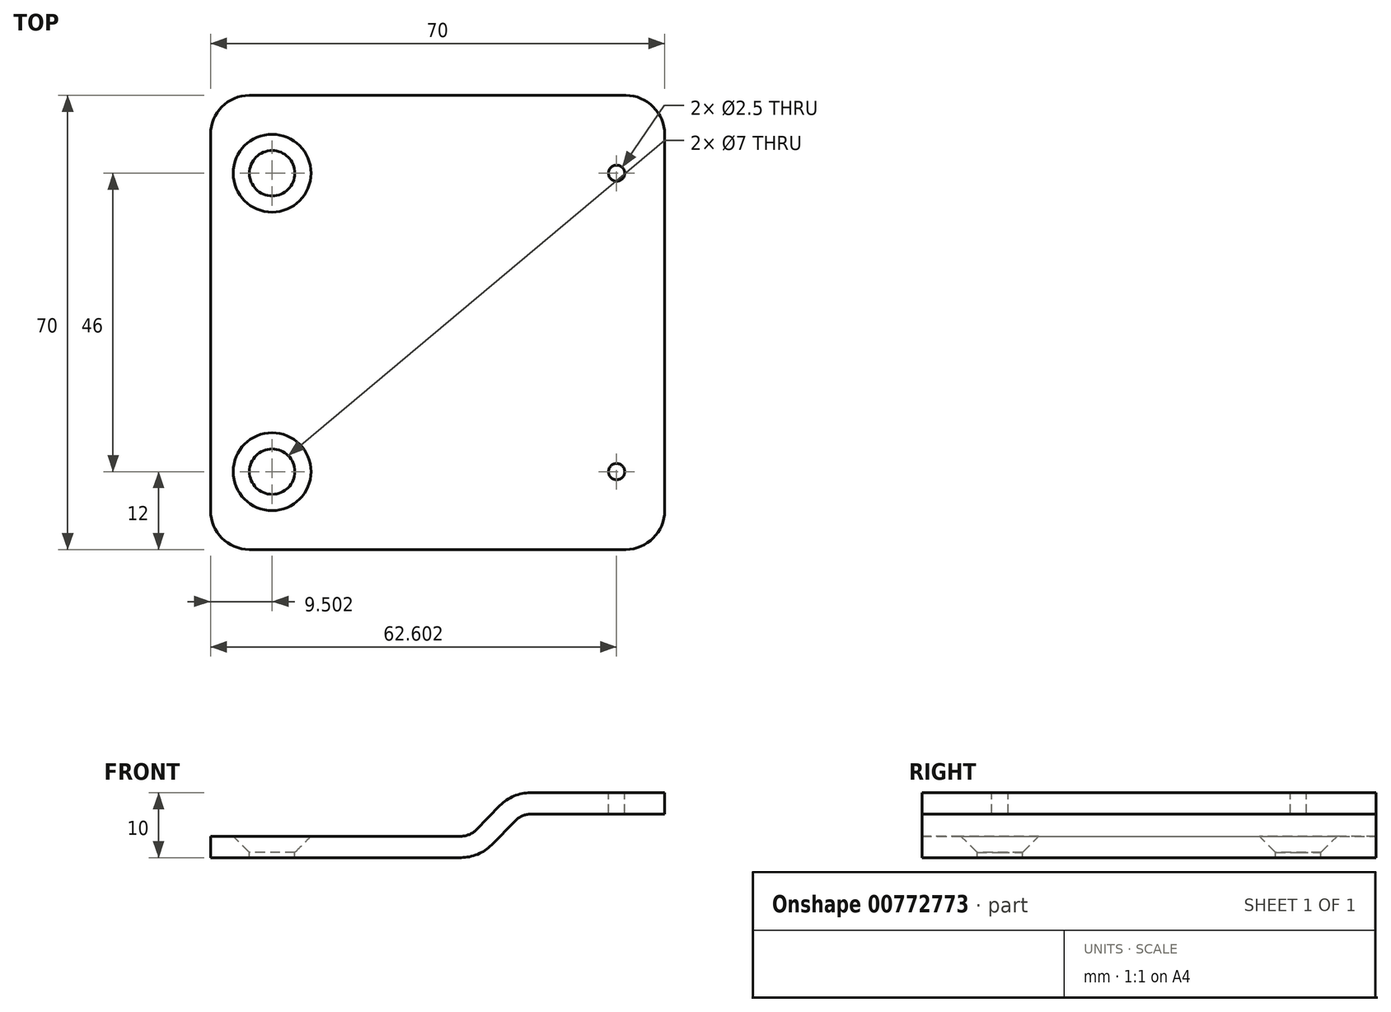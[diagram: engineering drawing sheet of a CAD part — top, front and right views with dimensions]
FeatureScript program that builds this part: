
annotation { "Feature Type Name" : "Feature", "Feature Type Description" : "" }
export const myFeature = defineFeature(function(context is Context, id is Id, definition is map)
    precondition{}
    {
        {
            var Q0;
            Q0=qCreatedBy(makeId("Front.planeOp"),FACE);
            var sketch = newSketch(context, id + "F0", { "sketchPlane" : qUnion([Q0])});
            skLineSegment(sketch, "E0", {"start": v(-30.2, 0) * mm, "end": v(-30.2, 3.3) * mm});
            skLineSegment(sketch, "E1", {"start": v(-30.2, 3.3) * mm, "end": v(8.41, 3.3) * mm});
            skLineSegment(sketch, "E2", {"start": v(10.77, 4.3) * mm, "end": v(14.42, 8.02) * mm});
            skLineSegment(sketch, "E3", {"start": v(19.14, 10) * mm, "end": v(39.8, 10) * mm});
            skLineSegment(sketch, "E4", {"start": v(39.8, 10) * mm, "end": v(39.8, 6.7) * mm});
            skLineSegment(sketch, "E5", {"start": v(-30.2, 0) * mm, "end": v(8.42, 0) * mm});
            skLineSegment(sketch, "E6", {"start": v(13.12, 1.96) * mm, "end": v(16.83, 5.72) * mm});
            skLineSegment(sketch, "E7", {"start": v(39.8, 6.7) * mm, "end": v(19.18, 6.7) * mm});
            skPoint(sketch, "E8.visualSharp", {"position": v(17.8, 6.7) * mm});
            skArc(sketch, "E8.filletArc", {"start": v(19.18, 6.7) * mm, "mid": v(17.9, 6.45) * mm, "end": v(16.83, 5.72) * mm});
            skPoint(sketch, "E9.visualSharp", {"position": v(9.8, 3.3) * mm});
            skArc(sketch, "E9.filletArc", {"start": v(8.41, 3.3) * mm, "mid": v(9.7, 3.56) * mm, "end": v(10.77, 4.3) * mm});
            skPoint(sketch, "E10.visualSharp", {"position": v(16.36, 10) * mm});
            skArc(sketch, "E10.filletArc", {"start": v(19.14, 10) * mm, "mid": v(16.58, 9.48) * mm, "end": v(14.42, 8.02) * mm});
            skPoint(sketch, "E11.visualSharp", {"position": v(11.18, 0) * mm});
            skArc(sketch, "E11.filletArc", {"start": v(8.42, 0) * mm, "mid": v(10.97, 0.5) * mm, "end": v(13.12, 1.96) * mm});
            skSolve(sketch);
        }
        {
            var Q0;
            Q0 = qSketchRegion(id + "F0", true);
            extrude(context, id + "F1", {"entities" : qUnion([Q0]), "depth" : 70 * mm, "offsetDistance" : 25 * mm});
        }
        {
            var Q0;
            Q0=makeQuery(id+"F1.opExtrude","CAP_EDGE",EDGE,{"disambiguationData":[OSD([sQuery(id+"F0.wireOp",EDGE,"E0")])],"isStart":true});
            var Q1;
            Q1=makeQuery(id+"F1.opExtrude","CAP_EDGE",EDGE,{"disambiguationData":[OSD([sQuery(id+"F0.wireOp",EDGE,"E0")])],"isStart":false});
            var Q2;
            Q2=makeQuery(id+"F1.opExtrude","CAP_EDGE",EDGE,{"disambiguationData":[OSD([sQuery(id+"F0.wireOp",EDGE,"E4")])],"isStart":false});
            var Q3;
            Q3=makeQuery(id+"F1.opExtrude","CAP_EDGE",EDGE,{"disambiguationData":[OSD([sQuery(id+"F0.wireOp",EDGE,"E4")])],"isStart":true});
            fillet(context, id + "F2", {"entities" : qUnion([Q0, Q1, Q2, Q3]), "radius" : 6 * mm, "tangentPropagation" : true, "allowEdgeOverflow" : false});
        }
        {
            var Q0;
            Q0=makeQuery(id+"F1.opExtrude","SWEPT_FACE",FACE,{"disambiguationData":[OSD([sQuery(id+"F0.wireOp",EDGE,"E3")])]});
            var sketch = newSketch(context, id + "F3", { "sketchPlane" : qUnion([Q0])});
            skPoint(sketch, "E12", {"position": v(32.4, -12) * mm});
            skPoint(sketch, "E13", {"position": v(32.4, -58) * mm});
            skSolve(sketch);
        }
        {
            var Q0;
            Q0=sQuery(id+"F3.wireOp",VERTEX,"E12");
            var Q1;
            Q1=sQuery(id+"F3.wireOp",VERTEX,"E13");
            var Q2;
            Q2=makeQuery(id+"F1.opExtrude","SWEPT_BODY",BODY,{"disambiguationData":[OSD([sQuery(id+"F0.wireOp",EDGE,"E0"),sQuery(id+"F0.wireOp",EDGE,"E1"),sQuery(id+"F0.wireOp",EDGE,"E2"),sQuery(id+"F0.wireOp",EDGE,"E3"),sQuery(id+"F0.wireOp",EDGE,"E4"),sQuery(id+"F0.wireOp",EDGE,"E5"),sQuery(id+"F0.wireOp",EDGE,"E6"),sQuery(id+"F0.wireOp",EDGE,"E7"),sQuery(id+"F0.wireOp",EDGE,"E8.filletArc"),sQuery(id+"F0.wireOp",EDGE,"E9.filletArc"),sQuery(id+"F0.wireOp",EDGE,"E10.filletArc"),sQuery(id+"F0.wireOp",EDGE,"E11.filletArc")])]});
            hole(context, id + "F4", {"style" : HoleStyle.SIMPLE, "endStyle" : HoleEndStyle.THROUGH, "standardTappedOrClearance" : lookupTablePath({ "standard" : "ISO", "engagement" : "75%", "pitch" : "0.5 mm", "size" : "M3", "type" : "Tapped" }), "standardBlindInLast" : lookupTablePath({ "standard" : "ISO", "engagement" : "75%", "pitch" : "0.5 mm", "size" : "M3", "type" : "Tapped" }), "holeDiameter" : 2.5 * mm, "majorDiameter" : 3 * mm, "showTappedDepth" : true, "isTappedThrough" : true, "tappedDepth" : 12 * mm, "tapClearance" : 3, "locations" : qUnion([Q0, Q1]), "scope" : qUnion([Q2])});
        }
        {
            var Q0;
            Q0=makeQuery(id+"F1.opExtrude","SWEPT_FACE",FACE,{"disambiguationData":[OSD([sQuery(id+"F0.wireOp",EDGE,"E1")])]});
            var sketch = newSketch(context, id + "F5", { "sketchPlane" : qUnion([Q0])});
            skPoint(sketch, "E14", {"position": v(-20.7, -12) * mm});
            skPoint(sketch, "E15", {"position": v(-20.7, -58) * mm});
            skSolve(sketch);
        }
        {
            var Q0;
            Q0=sQuery(id+"F5.wireOp",VERTEX,"E14");
            var Q1;
            Q1=sQuery(id+"F5.wireOp",VERTEX,"E15");
            var Q2;
            Q2=makeQuery(id+"F1.opExtrude","SWEPT_BODY",BODY,{"disambiguationData":[OSD([sQuery(id+"F0.wireOp",EDGE,"E0"),sQuery(id+"F0.wireOp",EDGE,"E1"),sQuery(id+"F0.wireOp",EDGE,"E2"),sQuery(id+"F0.wireOp",EDGE,"E3"),sQuery(id+"F0.wireOp",EDGE,"E4"),sQuery(id+"F0.wireOp",EDGE,"E5"),sQuery(id+"F0.wireOp",EDGE,"E6"),sQuery(id+"F0.wireOp",EDGE,"E7"),sQuery(id+"F0.wireOp",EDGE,"E8.filletArc"),sQuery(id+"F0.wireOp",EDGE,"E9.filletArc"),sQuery(id+"F0.wireOp",EDGE,"E10.filletArc"),sQuery(id+"F0.wireOp",EDGE,"E11.filletArc")])]});
            hole(context, id + "F6", {"style" : HoleStyle.C_SINK, "endStyle" : HoleEndStyle.THROUGH, "holeDiameter" : 7 * mm, "cSinkDiameter" : 12 * mm, "cSinkAngle" : 90 * degree, "majorDiameter" : 3 * mm, "isTappedThrough" : true, "tappedDepth" : 12 * mm, "tapClearance" : 3, "locations" : qUnion([Q0, Q1]), "scope" : qUnion([Q2])});
        }
    });
